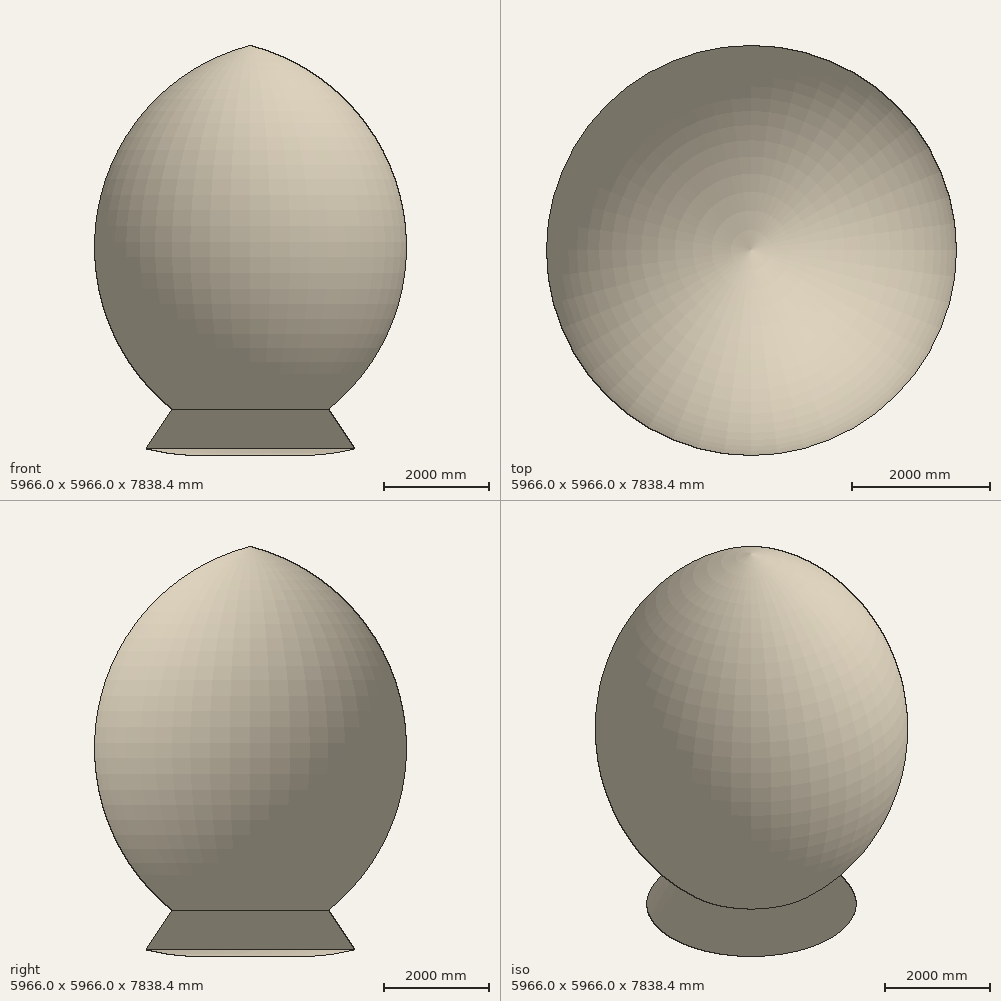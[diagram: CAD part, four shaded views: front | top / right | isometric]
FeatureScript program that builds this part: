
annotation { "Feature Type Name" : "Feature", "Feature Type Description" : "" }
export const myFeature = defineFeature(function(context is Context, id is Id, definition is map)
    precondition{}
    {
        {
            var Q0;
            Q0=qCreatedBy(makeId("Front.planeOp"),FACE);
            var sketch = newSketch(context, id + "F0", { "sketchPlane" : qUnion([Q0])});
            skLineSegment(sketch, "E0", {"start": v(0, 1954.86) * mm, "end": v(0, -1045.14) * mm});
            skArc(sketch, "E1", {"start": v(0, -1045.14) * mm, "mid": v(1000, -1172.72) * mm, "end": v(2000, -1045.14) * mm});
            skLineSegment(sketch, "E2", {"start": v(0, 1954.86) * mm, "end": v(2000, -1045.14) * mm});
            skSolve(sketch);
        }
        {
            var Q0;
            Q0=makeQuery(id+"F0.imprint","IMPRINT",FACE,{"disambiguationData":[TD([[makeQuery(id+"F0.imprint","IMPRINT",EDGE,{"derivedFrom":sQuery(id+"F0.wireOp",EDGE,"E0")}),1.0]])]});
            var Q1;
            Q1=sQuery(id+"F0.wireOp",EDGE,"E0");
            revolve(context, id + "F1", {"entities" : qUnion([Q0]), "axis" : qUnion([Q1]), "revolveType" : RevolveType.FULL});
        }
    });
